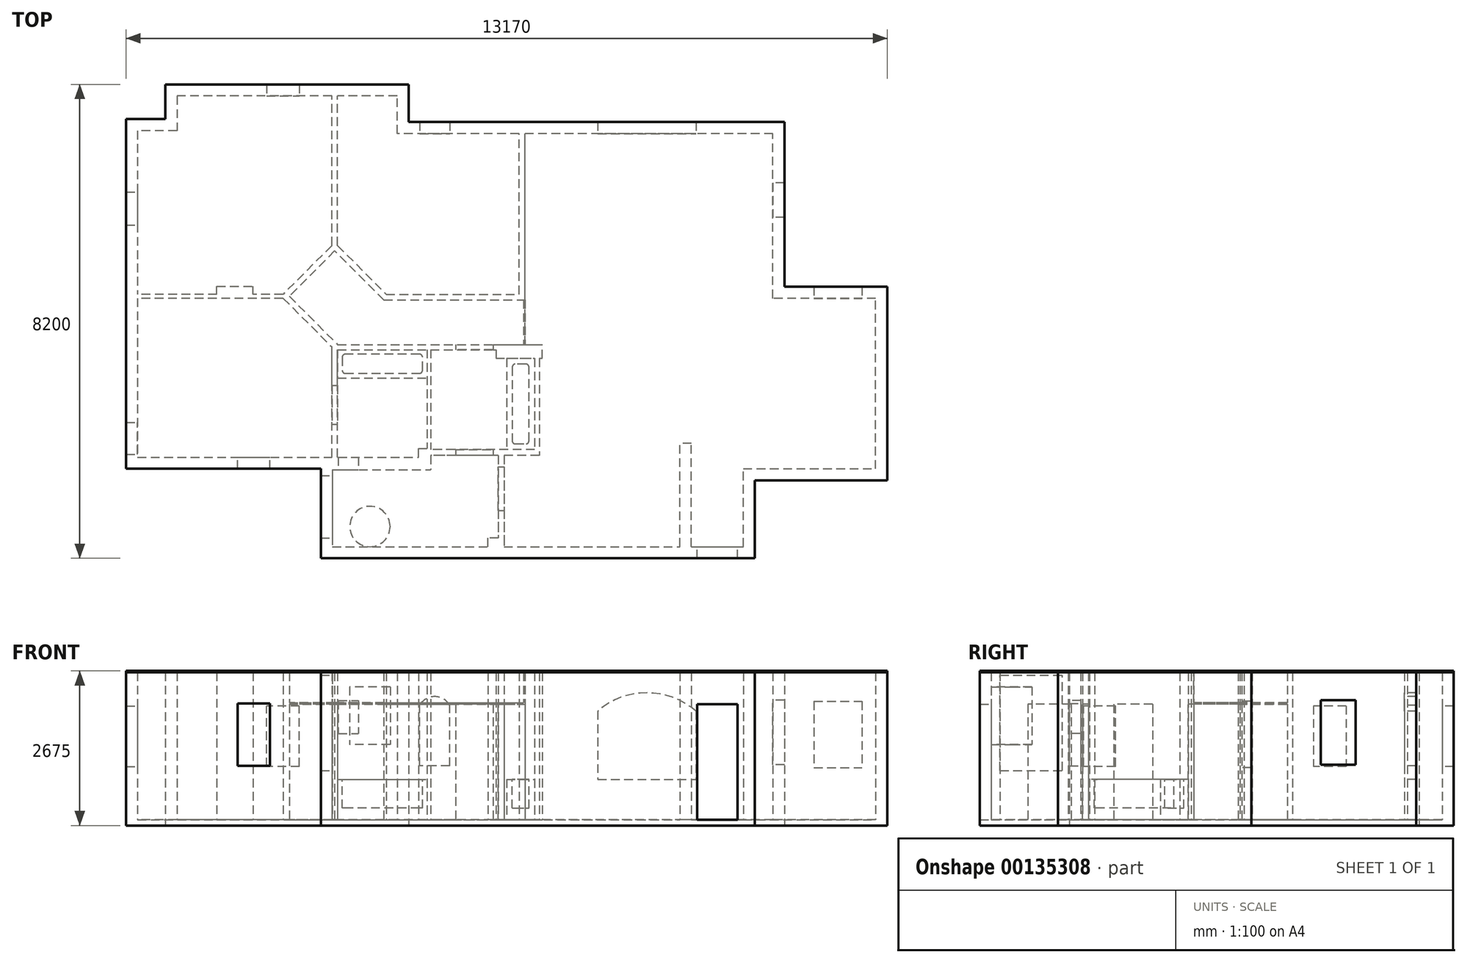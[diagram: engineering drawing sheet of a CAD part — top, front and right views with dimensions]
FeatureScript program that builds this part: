
annotation { "Feature Type Name" : "Feature", "Feature Type Description" : "" }
export const myFeature = defineFeature(function(context is Context, id is Id, definition is map)
    precondition{}
    {
        {
            var Q0;
            Q0=qCreatedBy(makeId("Top.planeOp"),FACE);
            var sketch = newSketch(context, id + "F0", { "sketchPlane" : qUnion([Q0])});
            skLineSegment(sketch, "E0", {"start": v(0, 0) * mm, "end": v(0, 1350) * mm});
            skLineSegment(sketch, "E1", {"start": v(0, 1350) * mm, "end": v(2290, 1350) * mm});
            skLineSegment(sketch, "E2", {"start": v(2290, 1350) * mm, "end": v(2290, 4300) * mm});
            skLineSegment(sketch, "E3", {"start": v(2290, 4300) * mm, "end": v(510, 4300) * mm});
            skLineSegment(sketch, "E4", {"start": v(510, 4300) * mm, "end": v(510, 7150) * mm});
            skLineSegment(sketch, "E5", {"start": v(510, 7150) * mm, "end": v(-5990, 7150) * mm});
            skLineSegment(sketch, "E6", {"start": v(-5990, 7150) * mm, "end": v(-5990, 7800) * mm});
            skLineSegment(sketch, "E7", {"start": v(-5990, 7800) * mm, "end": v(-9800, 7800) * mm});
            skLineSegment(sketch, "E8", {"start": v(-9800, 7800) * mm, "end": v(-9800, 7200) * mm});
            skLineSegment(sketch, "E9", {"start": v(-9800, 7200) * mm, "end": v(-10480, 7200) * mm});
            skLineSegment(sketch, "E10", {"start": v(-10480, 7200) * mm, "end": v(-10480, 1550) * mm});
            skLineSegment(sketch, "E11", {"start": v(-10480, 1550) * mm, "end": v(-7110, 1550) * mm});
            skLineSegment(sketch, "E12", {"start": v(-7110, 1550) * mm, "end": v(-7110, 0) * mm});
            skLineSegment(sketch, "E13", {"start": v(-7110, 0) * mm, "end": v(0, 0) * mm});
            skLineSegment(sketch, "E14.0", {"start": v(-5790, 7350) * mm, "end": v(-5790, 8000) * mm});
            skLineSegment(sketch, "E14.1", {"start": v(710, 7350) * mm, "end": v(-5790, 7350) * mm});
            skLineSegment(sketch, "E14.2", {"start": v(710, 4500) * mm, "end": v(710, 7350) * mm});
            skLineSegment(sketch, "E14.3", {"start": v(-10680, 1350) * mm, "end": v(-7310, 1350) * mm});
            skLineSegment(sketch, "E14.4", {"start": v(-10680, 7400) * mm, "end": v(-10680, 1350) * mm});
            skLineSegment(sketch, "E14.5", {"start": v(-10000, 7400) * mm, "end": v(-10680, 7400) * mm});
            skLineSegment(sketch, "E14.6", {"start": v(-10000, 8000) * mm, "end": v(-10000, 7400) * mm});
            skLineSegment(sketch, "E14.7", {"start": v(-7310, 1350) * mm, "end": v(-7310, -200) * mm});
            skLineSegment(sketch, "E14.8", {"start": v(-7310, -200) * mm, "end": v(200, -200) * mm});
            skLineSegment(sketch, "E14.9", {"start": v(200, -200) * mm, "end": v(200, 1150) * mm});
            skLineSegment(sketch, "E14.10", {"start": v(-5790, 8000) * mm, "end": v(-10000, 8000) * mm});
            skLineSegment(sketch, "E14.11", {"start": v(200, 1150) * mm, "end": v(2490, 1150) * mm});
            skLineSegment(sketch, "E14.12", {"start": v(2490, 1150) * mm, "end": v(2490, 4500) * mm});
            skLineSegment(sketch, "E14.13", {"start": v(2490, 4500) * mm, "end": v(710, 4500) * mm});
            skSolve(sketch);
        }
        {
            var Q0;
            Q0=makeQuery(id+"F0.imprint","IMPRINT",FACE,{"disambiguationData":[TD([[makeQuery(id+"F0.imprint","IMPRINT",EDGE,{"derivedFrom":sQuery(id+"F0.wireOp",EDGE,"E0")}),-1.0]])]});
            extrude(context, id + "F1", {"entities" : qUnion([Q0]), "depth" : 2550 * mm});
        }
        {
            var Q0;
            Q0=makeQuery(id+"F1.opExtrude","CAP_FACE",FACE,{"disambiguationData":[OSD([sQuery(id+"F0.wireOp",EDGE,"E0"),sQuery(id+"F0.wireOp",EDGE,"E1"),sQuery(id+"F0.wireOp",EDGE,"E2"),sQuery(id+"F0.wireOp",EDGE,"E3"),sQuery(id+"F0.wireOp",EDGE,"E4"),sQuery(id+"F0.wireOp",EDGE,"E5"),sQuery(id+"F0.wireOp",EDGE,"E6"),sQuery(id+"F0.wireOp",EDGE,"E7"),sQuery(id+"F0.wireOp",EDGE,"E8"),sQuery(id+"F0.wireOp",EDGE,"E9"),sQuery(id+"F0.wireOp",EDGE,"E10"),sQuery(id+"F0.wireOp",EDGE,"E11"),sQuery(id+"F0.wireOp",EDGE,"E12"),sQuery(id+"F0.wireOp",EDGE,"E13"),sQuery(id+"F0.wireOp",EDGE,"E14.0"),sQuery(id+"F0.wireOp",EDGE,"E14.1"),sQuery(id+"F0.wireOp",EDGE,"E14.2"),sQuery(id+"F0.wireOp",EDGE,"E14.3"),sQuery(id+"F0.wireOp",EDGE,"E14.4"),sQuery(id+"F0.wireOp",EDGE,"E14.5"),sQuery(id+"F0.wireOp",EDGE,"E14.6"),sQuery(id+"F0.wireOp",EDGE,"E14.7"),sQuery(id+"F0.wireOp",EDGE,"E14.8"),sQuery(id+"F0.wireOp",EDGE,"E14.9"),sQuery(id+"F0.wireOp",EDGE,"E14.10"),sQuery(id+"F0.wireOp",EDGE,"E14.11"),sQuery(id+"F0.wireOp",EDGE,"E14.12"),sQuery(id+"F0.wireOp",EDGE,"E14.13")])],"isStart":true});
            var sketch = newSketch(context, id + "F2", { "sketchPlane" : qUnion([Q0])});
            skLineSegment(sketch, "E15.0", {"start": v(-10000, -7400) * mm, "end": v(-10680, -7400) * mm});
            skLineSegment(sketch, "E15.1", {"start": v(-10680, -7400) * mm, "end": v(-10680, -1350) * mm});
            skLineSegment(sketch, "E15.2", {"start": v(-10680, -1350) * mm, "end": v(-7310, -1350) * mm});
            skLineSegment(sketch, "E15.3", {"start": v(-7310, -1350) * mm, "end": v(-7310, 200) * mm});
            skLineSegment(sketch, "E15.4", {"start": v(-7310, 200) * mm, "end": v(200, 200) * mm});
            skLineSegment(sketch, "E15.5", {"start": v(200, 200) * mm, "end": v(200, -1150) * mm});
            skLineSegment(sketch, "E15.6", {"start": v(200, -1150) * mm, "end": v(2490, -1150) * mm});
            skLineSegment(sketch, "E15.7", {"start": v(2490, -1150) * mm, "end": v(2490, -4500) * mm});
            skLineSegment(sketch, "E15.8", {"start": v(2490, -4500) * mm, "end": v(710, -4500) * mm});
            skLineSegment(sketch, "E15.9", {"start": v(710, -4500) * mm, "end": v(710, -7350) * mm});
            skLineSegment(sketch, "E15.10", {"start": v(710, -7350) * mm, "end": v(-5790, -7350) * mm});
            skLineSegment(sketch, "E15.11", {"start": v(-5790, -7350) * mm, "end": v(-5790, -8000) * mm});
            skLineSegment(sketch, "E15.12", {"start": v(-5790, -8000) * mm, "end": v(-10000, -8000) * mm});
            skLineSegment(sketch, "E15.13", {"start": v(-10000, -8000) * mm, "end": v(-10000, -7400) * mm});
            skSolve(sketch);
        }
        {
            var Q0;
            Q0=qSketchRegion(id+"F2",true);
            extrude(context, id + "F3", {"entities" : qUnion([Q0]), "operationType" : NewBodyOperationType.ADD, "depth" : 100 * mm});
        }
        {
            var Q0;
            Q0=qCreatedBy(makeId("Top.planeOp"),FACE);
            var sketch = newSketch(context, id + "F4", { "sketchPlane" : qUnion([Q0])});
            skLineSegment(sketch, "E16.right", {"start": v(-7120, 1550) * mm, "end": v(-7120, 3458.58) * mm});
            skLineSegment(sketch, "E17.bottom", {"start": v(-7961.42, 4370) * mm, "end": v(-10680, 4370) * mm});
            skLineSegment(sketch, "E17.top", {"start": v(-7961.42, 4300) * mm, "end": v(-10680, 4300) * mm});
            skLineSegment(sketch, "E18.trimOffspring", {"start": v(-7120, 5211.42) * mm, "end": v(-7120, 8000) * mm});
            skLineSegment(sketch, "E19", {"start": v(-6178.58, 4370) * mm, "end": v(-3880, 4370) * mm});
            skLineSegment(sketch, "E20", {"start": v(-3880, 4370) * mm, "end": v(-3880, 7350) * mm});
            skLineSegment(sketch, "E21.0", {"start": v(-3780, 4270) * mm, "end": v(-3780, 7350) * mm});
            skLineSegment(sketch, "E21.1", {"start": v(-6220, 4270) * mm, "end": v(-3780, 4270) * mm});
            skLineSegment(sketch, "E22.trimOffspring", {"start": v(-7020, 5211.42) * mm, "end": v(-7020, 8000) * mm});
            skLineSegment(sketch, "E23", {"start": v(-7020, 1550) * mm, "end": v(-7020, 3410) * mm});
            skLineSegment(sketch, "E24", {"start": v(-3880, 7350) * mm, "end": v(-3780, 7350) * mm});
            skLineSegment(sketch, "E25", {"start": v(-7120, 8000) * mm, "end": v(-7020, 8000) * mm});
            skLineSegment(sketch, "E26", {"start": v(-10680, 4370) * mm, "end": v(-10680, 4300) * mm});
            skLineSegment(sketch, "E27.bottom", {"start": v(-900, 0) * mm, "end": v(-1100, 0) * mm});
            skLineSegment(sketch, "E27.top", {"start": v(-900, 1790) * mm, "end": v(-1100, 1790) * mm});
            skLineSegment(sketch, "E27.left", {"start": v(-900, 0) * mm, "end": v(-900, 1790) * mm});
            skLineSegment(sketch, "E27.right", {"start": v(-1100, 0) * mm, "end": v(-1100, 1790) * mm});
            skLineSegment(sketch, "E28.bottom", {"start": v(-7020, 3500) * mm, "end": v(-3480, 3500) * mm});
            skLineSegment(sketch, "E28.top", {"start": v(-7020, 3410) * mm, "end": v(-4280, 3410) * mm});
            skLineSegment(sketch, "E29.bottom", {"start": v(-7020, 1550) * mm, "end": v(-5620, 1550) * mm});
            skLineSegment(sketch, "E29.top", {"start": v(-7110, 1330) * mm, "end": v(-5410, 1330) * mm});
            skLineSegment(sketch, "E29.left", {"start": v(-7110, 1550) * mm, "end": v(-7110, 1330) * mm});
            skLineSegment(sketch, "E29.right", {"start": v(-5410, 1550) * mm, "end": v(-5410, 1330) * mm});
            skLineSegment(sketch, "E30.bottom", {"start": v(-5410, 3410) * mm, "end": v(-5470, 3410) * mm});
            skLineSegment(sketch, "E30.left", {"start": v(-5410, 3410) * mm, "end": v(-5410, 1680) * mm});
            skLineSegment(sketch, "E30.right", {"start": v(-5470, 3410) * mm, "end": v(-5470, 1700) * mm});
            skLineSegment(sketch, "E31.top", {"start": v(-3610, 1680) * mm, "end": v(-3530, 1680) * mm});
            skLineSegment(sketch, "E31.left", {"start": v(-3610, 3260) * mm, "end": v(-3610, 1680) * mm});
            skLineSegment(sketch, "E31.right", {"start": v(-3530, 3260) * mm, "end": v(-3530, 1680) * mm});
            skLineSegment(sketch, "E32.bottom", {"start": v(-3530, 1680) * mm, "end": v(-5410, 1680) * mm});
            skLineSegment(sketch, "E32.top", {"start": v(-3530, 1580) * mm, "end": v(-5410, 1580) * mm});
            skLineSegment(sketch, "E32.left", {"start": v(-3530, 1680) * mm, "end": v(-3530, 1580) * mm});
            skLineSegment(sketch, "E33.bottom", {"start": v(-9110, 4370) * mm, "end": v(-8480, 4370) * mm});
            skLineSegment(sketch, "E33.top", {"start": v(-9110, 4510) * mm, "end": v(-8480, 4510) * mm});
            skLineSegment(sketch, "E33.left", {"start": v(-9110, 4370) * mm, "end": v(-9110, 4510) * mm});
            skLineSegment(sketch, "E33.right", {"start": v(-8480, 4370) * mm, "end": v(-8480, 4510) * mm});
            skLineSegment(sketch, "E34.top", {"start": v(-4280, 3260) * mm, "end": v(-3610, 3260) * mm});
            skLineSegment(sketch, "E34.left", {"start": v(-4280, 3410) * mm, "end": v(-4280, 3260) * mm});
            skLineSegment(sketch, "E35.trimOffspring", {"start": v(-3530, 3260) * mm, "end": v(-3480, 3260) * mm});
            skLineSegment(sketch, "E36.trimOffspring", {"start": v(-5410, 1580) * mm, "end": v(-5410, 1550) * mm});
            skLineSegment(sketch, "E37.bottom", {"start": v(-4240, 1580) * mm, "end": v(-4140, 1580) * mm});
            skLineSegment(sketch, "E37.left", {"start": v(-4240, 1580) * mm, "end": v(-4240, 150) * mm});
            skLineSegment(sketch, "E37.right", {"start": v(-4140, 1580) * mm, "end": v(-4140, 0) * mm});
            skLineSegment(sketch, "E38.top", {"start": v(-4240, 150) * mm, "end": v(-4420, 150) * mm});
            skLineSegment(sketch, "E38.right", {"start": v(-4420, 0) * mm, "end": v(-4420, 150) * mm});
            skLineSegment(sketch, "E39", {"start": v(-4420, 0) * mm, "end": v(-4140, 0) * mm});
            skLineSegment(sketch, "E40", {"start": v(-7120, 1550) * mm, "end": v(-7110, 1550) * mm});
            skLineSegment(sketch, "E41", {"start": v(-7020, 5211.42) * mm, "end": v(-6178.58, 4370) * mm});
            skLineSegment(sketch, "E42", {"start": v(-7120, 5211.42) * mm, "end": v(-7961.42, 4370) * mm});
            skLineSegment(sketch, "E43", {"start": v(-7961.42, 4300) * mm, "end": v(-7120, 3458.58) * mm});
            skLineSegment(sketch, "E44", {"start": v(-6220, 4270) * mm, "end": v(-7070, 5120) * mm});
            skLineSegment(sketch, "E45", {"start": v(-7070, 5120) * mm, "end": v(-7855, 4335) * mm});
            skLineSegment(sketch, "E46", {"start": v(-7855, 4335) * mm, "end": v(-7020, 3500) * mm});
            skLineSegment(sketch, "E47", {"start": v(-7961.42, 4370) * mm, "end": v(-7961.42, 4300) * mm, "construction": true});
            skLineSegment(sketch, "E48", {"start": v(-7961.42, 4335) * mm, "end": v(-7620.59, 4335) * mm, "construction": true});
            skLineSegment(sketch, "E49", {"start": v(-3480, 3260) * mm, "end": v(-3480, 3500) * mm});
            skLineSegment(sketch, "E50", {"start": v(-5620, 1550) * mm, "end": v(-5620, 1700) * mm});
            skLineSegment(sketch, "E51", {"start": v(-5620, 1700) * mm, "end": v(-5470, 1700) * mm});
            skSolve(sketch);
        }
        {
            var Q0;
            Q0=qSketchRegion(id+"F4",true);
            extrude(context, id + "F5", {"entities" : qUnion([Q0]), "operationType" : NewBodyOperationType.ADD, "depth" : 2550 * mm});
        }
        {
            var Q0;
            Q0=makeQuery(id+"F1.opExtrude","SWEPT_FACE",FACE,{"disambiguationData":[OSD([sQuery(id+"F0.wireOp",EDGE,"E3")])]});
            var sketch = newSketch(context, id + "F6", { "sketchPlane" : qUnion([Q0])});
            skLineSegment(sketch, "E52.bottom", {"start": v(1220, 2050) * mm, "end": v(2050, 2050) * mm});
            skLineSegment(sketch, "E52.top", {"start": v(1220, 900) * mm, "end": v(2050, 900) * mm});
            skLineSegment(sketch, "E52.left", {"start": v(1220, 2050) * mm, "end": v(1220, 900) * mm});
            skLineSegment(sketch, "E52.right", {"start": v(2050, 2050) * mm, "end": v(2050, 900) * mm});
            skSolve(sketch);
        }
        {
            var Q0;
            Q0=qSketchRegion(id+"F6",true);
            extrude(context, id + "F7", {"entities" : qUnion([Q0]), "operationType" : NewBodyOperationType.REMOVE, "endBound" : BoundingType.THROUGH_ALL, "oppositeDirection" : true, "depth" : 25 * mm});
        }
        {
            var Q0;
            Q0=makeQuery(id+"F1.opExtrude","SWEPT_FACE",FACE,{"disambiguationData":[OSD([sQuery(id+"F0.wireOp",EDGE,"E4")])]});
            var sketch = newSketch(context, id + "F8", { "sketchPlane" : qUnion([Q0])});
            skLineSegment(sketch, "E53.bottom", {"start": v(-6300, 950) * mm, "end": v(-5700, 950) * mm});
            skLineSegment(sketch, "E53.top", {"start": v(-6300, 2070) * mm, "end": v(-5700, 2070) * mm});
            skLineSegment(sketch, "E53.left", {"start": v(-6300, 950) * mm, "end": v(-6300, 2070) * mm});
            skLineSegment(sketch, "E53.right", {"start": v(-5700, 950) * mm, "end": v(-5700, 2070) * mm});
            skSolve(sketch);
        }
        {
            var Q0;
            Q0=qSketchRegion(id+"F8",true);
            extrude(context, id + "F9", {"entities" : qUnion([Q0]), "operationType" : NewBodyOperationType.REMOVE, "endBound" : BoundingType.UP_TO_NEXT, "oppositeDirection" : true, "depth" : 25 * mm});
        }
        {
            var Q0;
            {var subQ1=sQuery(id+"F0.wireOp",EDGE,"E4");var subQ2=sQuery(id+"F0.wireOp",EDGE,"E5");Q0=makeQuery(id+"F5.boolean.opBoolean","SPLIT",FACE,{"disambiguationData":[TD([makeQuery(id+"F1.opExtrude","SWEPT_FACE",FACE,{"disambiguationData":[OSD([subQ1])]})])],"derivedFrom":makeQuery(id+"F1.opExtrude","SWEPT_FACE",FACE,{"disambiguationData":[OSD([subQ2])]})});}
            var sketch = newSketch(context, id + "F10", { "sketchPlane" : qUnion([Q0])});
            skLineSegment(sketch, "E54.top", {"start": v(-2520, 700) * mm, "end": v(-820, 700) * mm});
            skLineSegment(sketch, "E54.left", {"start": v(-2520, 1880) * mm, "end": v(-2520, 700) * mm});
            skLineSegment(sketch, "E54.right", {"start": v(-820, 1880) * mm, "end": v(-820, 700) * mm});
            skArc(sketch, "E55", {"start": v(-820, 1880) * mm, "mid": v(-1670, 2196.38) * mm, "end": v(-2520, 1880) * mm});
            skSolve(sketch);
        }
        {
            var Q0;
            Q0=qSketchRegion(id+"F10",true);
            extrude(context, id + "F11", {"entities" : qUnion([Q0]), "operationType" : NewBodyOperationType.REMOVE, "endBound" : BoundingType.UP_TO_NEXT, "oppositeDirection" : true, "depth" : 25 * mm});
        }
        {
            var Q0;
            {var subQ1=sQuery(id+"F0.wireOp",EDGE,"E6");var subQ2=sQuery(id+"F0.wireOp",EDGE,"E5");Q0=makeQuery(id+"F5.boolean.opBoolean","SPLIT",FACE,{"disambiguationData":[TD([makeQuery(id+"F1.opExtrude","SWEPT_FACE",FACE,{"disambiguationData":[OSD([subQ1])]})])],"derivedFrom":makeQuery(id+"F1.opExtrude","SWEPT_FACE",FACE,{"disambiguationData":[OSD([subQ2])]})});}
            var sketch = newSketch(context, id + "F12", { "sketchPlane" : qUnion([Q0])});
            skLineSegment(sketch, "E56.top", {"start": v(-5600, 930) * mm, "end": v(-5080, 930) * mm});
            skLineSegment(sketch, "E56.left", {"start": v(-5600, 1980) * mm, "end": v(-5600, 930) * mm});
            skLineSegment(sketch, "E56.right", {"start": v(-5080, 1980) * mm, "end": v(-5080, 930) * mm});
            skArc(sketch, "E57", {"start": v(-5080, 1980) * mm, "mid": v(-5340, 2130.33) * mm, "end": v(-5600, 1980) * mm});
            skSolve(sketch);
        }
        {
            var Q0;
            Q0=qSketchRegion(id+"F12",true);
            extrude(context, id + "F13", {"entities" : qUnion([Q0]), "operationType" : NewBodyOperationType.REMOVE, "endBound" : BoundingType.UP_TO_NEXT, "oppositeDirection" : true, "depth" : 25 * mm});
        }
        {
            var Q0;
            {var subQ1=sQuery(id+"F0.wireOp",EDGE,"E8");var subQ2=sQuery(id+"F0.wireOp",EDGE,"E7");Q0=makeQuery(id+"F5.boolean.opBoolean","SPLIT",FACE,{"disambiguationData":[TD([makeQuery(id+"F1.opExtrude","SWEPT_FACE",FACE,{"disambiguationData":[OSD([subQ1])]})])],"derivedFrom":makeQuery(id+"F1.opExtrude","SWEPT_FACE",FACE,{"disambiguationData":[OSD([subQ2])]})});}
            var sketch = newSketch(context, id + "F14", { "sketchPlane" : qUnion([Q0])});
            skLineSegment(sketch, "E58.bottom", {"start": v(-8250, 1970) * mm, "end": v(-7680, 1970) * mm});
            skLineSegment(sketch, "E58.top", {"start": v(-8250, 920) * mm, "end": v(-7680, 920) * mm});
            skLineSegment(sketch, "E58.left", {"start": v(-8250, 1970) * mm, "end": v(-8250, 920) * mm});
            skLineSegment(sketch, "E58.right", {"start": v(-7680, 1970) * mm, "end": v(-7680, 920) * mm});
            skSolve(sketch);
        }
        {
            var Q0;
            Q0=qSketchRegion(id+"F14",true);
            extrude(context, id + "F15", {"entities" : qUnion([Q0]), "operationType" : NewBodyOperationType.REMOVE, "endBound" : BoundingType.UP_TO_NEXT, "oppositeDirection" : true, "depth" : 25 * mm});
        }
        {
            var Q0;
            {var subQ3=sQuery(id+"F0.wireOp",EDGE,"E9");var subQ4=sQuery(id+"F0.wireOp",EDGE,"E10");Q0=makeQuery(id+"F5.boolean.opBoolean","SPLIT",FACE,{"disambiguationData":[TD([makeQuery(id+"F1.opExtrude","SWEPT_FACE",FACE,{"disambiguationData":[OSD([subQ3])]})])],"derivedFrom":makeQuery(id+"F1.opExtrude","SWEPT_FACE",FACE,{"disambiguationData":[OSD([subQ4])]})});}
            var sketch = newSketch(context, id + "F16", { "sketchPlane" : qUnion([Q0])});
            skLineSegment(sketch, "E59.bottom", {"start": v(6140, 1970) * mm, "end": v(5570, 1970) * mm});
            skLineSegment(sketch, "E59.top", {"start": v(6140, 920) * mm, "end": v(5570, 920) * mm});
            skLineSegment(sketch, "E59.left", {"start": v(6140, 1970) * mm, "end": v(6140, 920) * mm});
            skLineSegment(sketch, "E59.right", {"start": v(5570, 1970) * mm, "end": v(5570, 920) * mm});
            skSolve(sketch);
        }
        {
            var Q0;
            Q0=qSketchRegion(id+"F16",true);
            extrude(context, id + "F17", {"entities" : qUnion([Q0]), "operationType" : NewBodyOperationType.REMOVE, "endBound" : BoundingType.UP_TO_NEXT, "oppositeDirection" : true, "depth" : 25 * mm});
        }
        {
            var Q0;
            {var subQ4=sQuery(id+"F0.wireOp",EDGE,"E11");var subQ5=sQuery(id+"F0.wireOp",EDGE,"E10");Q0=makeQuery(id+"F5.boolean.opBoolean","SPLIT",FACE,{"disambiguationData":[TD([makeQuery(id+"F1.opExtrude","SWEPT_FACE",FACE,{"disambiguationData":[OSD([subQ4])]})])],"derivedFrom":makeQuery(id+"F1.opExtrude","SWEPT_FACE",FACE,{"disambiguationData":[OSD([subQ5])]})});}
            var sketch = newSketch(context, id + "F18", { "sketchPlane" : qUnion([Q0])});
            skLineSegment(sketch, "E60.bottom", {"start": v(1600, 1970) * mm, "end": v(2150, 1970) * mm});
            skLineSegment(sketch, "E60.top", {"start": v(1600, 920) * mm, "end": v(2150, 920) * mm});
            skLineSegment(sketch, "E60.left", {"start": v(1600, 1970) * mm, "end": v(1600, 920) * mm});
            skLineSegment(sketch, "E60.right", {"start": v(2150, 1970) * mm, "end": v(2150, 920) * mm});
            skSolve(sketch);
        }
        {
            var Q0;
            Q0=qSketchRegion(id+"F18",true);
            extrude(context, id + "F19", {"entities" : qUnion([Q0]), "operationType" : NewBodyOperationType.REMOVE, "endBound" : BoundingType.UP_TO_NEXT, "oppositeDirection" : true, "depth" : 25 * mm});
        }
        {
            var Q0;
            Q0=makeQuery(id+"F1.opExtrude","SWEPT_FACE",FACE,{"disambiguationData":[OSD([sQuery(id+"F0.wireOp",EDGE,"E11")])]});
            var sketch = newSketch(context, id + "F20", { "sketchPlane" : qUnion([Q0])});
            skLineSegment(sketch, "E61.bottom", {"start": v(8750, 2010) * mm, "end": v(8190, 2010) * mm});
            skLineSegment(sketch, "E61.top", {"start": v(8750, 930) * mm, "end": v(8190, 930) * mm});
            skLineSegment(sketch, "E61.left", {"start": v(8750, 2010) * mm, "end": v(8750, 930) * mm});
            skLineSegment(sketch, "E61.right", {"start": v(8190, 2010) * mm, "end": v(8190, 930) * mm});
            skSolve(sketch);
        }
        {
            var Q0;
            Q0=qSketchRegion(id+"F20",true);
            extrude(context, id + "F21", {"entities" : qUnion([Q0]), "operationType" : NewBodyOperationType.REMOVE, "endBound" : BoundingType.UP_TO_NEXT, "oppositeDirection" : true, "depth" : 25 * mm});
        }
        {
            var Q0;
            Q0=makeQuery(id+"F1.opExtrude","SWEPT_FACE",FACE,{"disambiguationData":[OSD([sQuery(id+"F0.wireOp",EDGE,"E12")])]});
            var sketch = newSketch(context, id + "F22", { "sketchPlane" : qUnion([Q0])});
            skLineSegment(sketch, "E62.bottom", {"start": v(1230, 2500) * mm, "end": v(150, 2500) * mm});
            skLineSegment(sketch, "E62.top", {"start": v(1230, 850) * mm, "end": v(150, 850) * mm});
            skLineSegment(sketch, "E62.left", {"start": v(1230, 2500) * mm, "end": v(1230, 850) * mm});
            skLineSegment(sketch, "E62.right", {"start": v(150, 2500) * mm, "end": v(150, 850) * mm});
            skSolve(sketch);
        }
        {
            var Q0;
            Q0=qSketchRegion(id+"F22",true);
            extrude(context, id + "F23", {"entities" : qUnion([Q0]), "operationType" : NewBodyOperationType.REMOVE, "endBound" : BoundingType.UP_TO_NEXT, "oppositeDirection" : true, "depth" : 25 * mm});
        }
        {
            var Q0;
            Q0=makeQuery(id+"F5.opExtrude","SWEPT_FACE",FACE,{"disambiguationData":[OSD([sQuery(id+"F4.wireOp",EDGE,"E29.top")])]});
            var sketch = newSketch(context, id + "F24", { "sketchPlane" : qUnion([Q0])});
            skLineSegment(sketch, "E63.bottom", {"start": v(-7010, 2060) * mm, "end": v(-6660, 2060) * mm});
            skLineSegment(sketch, "E63.top", {"start": v(-7010, 1490) * mm, "end": v(-6660, 1490) * mm});
            skLineSegment(sketch, "E63.left", {"start": v(-7010, 2060) * mm, "end": v(-7010, 1490) * mm});
            skLineSegment(sketch, "E63.right", {"start": v(-6660, 2060) * mm, "end": v(-6660, 1490) * mm});
            skSolve(sketch);
        }
        {
            var Q0;
            Q0=qSketchRegion(id+"F24",true);
            extrude(context, id + "F25", {"entities" : qUnion([Q0]), "operationType" : NewBodyOperationType.REMOVE, "endBound" : BoundingType.UP_TO_NEXT, "oppositeDirection" : true, "depth" : 25 * mm});
        }
        {
            var Q0;
            {var subQ0=sQuery(id+"F4.wireOp",EDGE,"E23");Q0=makeQuery(id+"F25.boolean.opBoolean","MERGE",FACE,{"derivedFrom":[makeQuery(id+"F5.opExtrude","SWEPT_FACE",FACE,{"disambiguationData":[OSD([subQ0]),TDD([makeQuery(id+"F4.imprint","IMPRINT",EDGE,{"disambiguationData":[TD([[makeQuery(id+"F4.imprint","INTERSECT",VERTEX,{"derivedFrom":[subQ0,sQuery(id+"F4.wireOp",EDGE,"E29.bottom")]}),-1.0]])],"derivedFrom":subQ0})])]}),makeQuery(id+"F25.opExtrude","SWEPT_FACE",FACE,{"disambiguationData":[OSD([sQuery(id+"F24.wireOp",EDGE,"E63.left")])]})]});}
            var sketch = newSketch(context, id + "F26", { "sketchPlane" : qUnion([Q0])});
            skLineSegment(sketch, "E64.bottom", {"start": v(2790, 2000) * mm, "end": v(2120, 2000) * mm});
            skLineSegment(sketch, "E64.top", {"start": v(2790, 0) * mm, "end": v(2120, 0) * mm});
            skLineSegment(sketch, "E64.left", {"start": v(2790, 2000) * mm, "end": v(2790, 0) * mm});
            skLineSegment(sketch, "E64.right", {"start": v(2120, 2000) * mm, "end": v(2120, 0) * mm});
            skSolve(sketch);
        }
        {
            var Q0;
            Q0=makeQuery(id+"F26.imprint","IMPRINT",FACE,{"disambiguationData":[TD([[makeQuery(id+"F26.imprint","IMPRINT",EDGE,{"derivedFrom":sQuery(id+"F26.wireOp",EDGE,"E64.bottom")}),1.0]])]});
            extrude(context, id + "F27", {"entities" : qUnion([Q0]), "operationType" : NewBodyOperationType.REMOVE, "endBound" : BoundingType.UP_TO_NEXT, "oppositeDirection" : true, "depth" : 25 * mm});
        }
        {
            var Q0;
            {var subQ0=sQuery(id+"F4.wireOp",EDGE,"E28.top");Q0=makeQuery(id+"F5.opExtrude","SWEPT_FACE",FACE,{"disambiguationData":[OSD([subQ0]),TDD([makeQuery(id+"F4.imprint","IMPRINT",EDGE,{"disambiguationData":[TD([[makeQuery(id+"F4.imprint","INTERSECT",VERTEX,{"derivedFrom":[subQ0,sQuery(id+"F4.wireOp",EDGE,"E30.bottom"),sQuery(id+"F4.wireOp",EDGE,"E30.left")]}),-1.0]])],"derivedFrom":subQ0})])]});}
            var sketch = newSketch(context, id + "F28", { "sketchPlane" : qUnion([Q0])});
            skLineSegment(sketch, "E65.bottom", {"start": v(-4980, 2000) * mm, "end": v(-4330, 2000) * mm});
            skLineSegment(sketch, "E65.top", {"start": v(-4980, 0) * mm, "end": v(-4330, 0) * mm});
            skLineSegment(sketch, "E65.left", {"start": v(-4980, 2000) * mm, "end": v(-4980, 0) * mm});
            skLineSegment(sketch, "E65.right", {"start": v(-4330, 2000) * mm, "end": v(-4330, 0) * mm});
            skSolve(sketch);
        }
        {
            var Q0;
            Q0=qSketchRegion(id+"F28",true);
            var Q1;
            Q1=makeQuery(id+"F5.opExtrude","SWEPT_FACE",FACE,{"disambiguationData":[OSD([sQuery(id+"F4.wireOp",EDGE,"E32.top")])]});
            extrude(context, id + "F29", {"entities" : qUnion([Q0]), "operationType" : NewBodyOperationType.REMOVE, "endBound" : BoundingType.UP_TO_NEXT, "oppositeDirection" : true, "depth" : 25 * mm, "hasSecondDirection" : true, "secondDirectionBound" : BoundingType.UP_TO_SURFACE, "secondDirectionOppositeDirection" : false, "secondDirectionBoundEntityFace" : qUnion([Q1]), "secondDirectionDepth" : 25 * mm});
        }
        {
            var Q0;
            {var subQ0=sQuery(id+"F0.wireOp",EDGE,"E13");var subQ1=sQuery(id+"F0.wireOp",EDGE,"E0");Q0=makeQuery(id+"F5.boolean.opBoolean","SPLIT",FACE,{"disambiguationData":[TD([makeQuery(id+"F1.opExtrude","SWEPT_FACE",FACE,{"disambiguationData":[OSD([subQ1])]})])],"derivedFrom":makeQuery(id+"F1.opExtrude","SWEPT_FACE",FACE,{"disambiguationData":[OSD([subQ0])]})});}
            var sketch = newSketch(context, id + "F30", { "sketchPlane" : qUnion([Q0])});
            skLineSegment(sketch, "E66.bottom", {"start": v(800, 2000) * mm, "end": v(100, 2000) * mm});
            skLineSegment(sketch, "E66.top", {"start": v(800, 0) * mm, "end": v(100, 0) * mm});
            skLineSegment(sketch, "E66.left", {"start": v(800, 2000) * mm, "end": v(800, 0) * mm});
            skLineSegment(sketch, "E66.right", {"start": v(100, 2000) * mm, "end": v(100, 0) * mm});
            skSolve(sketch);
        }
        {
            var Q0;
            Q0=makeQuery(id+"F30.imprint","IMPRINT",FACE,{"disambiguationData":[TD([[makeQuery(id+"F30.imprint","IMPRINT",EDGE,{"derivedFrom":sQuery(id+"F30.wireOp",EDGE,"E66.bottom")}),1.0]])]});
            extrude(context, id + "F31", {"entities" : qUnion([Q0]), "operationType" : NewBodyOperationType.REMOVE, "endBound" : BoundingType.UP_TO_NEXT, "oppositeDirection" : true, "depth" : 25 * mm});
        }
        {
            var Q0;
            Q0=makeQuery(id+"F5.opExtrude","SWEPT_FACE",FACE,{"disambiguationData":[OSD([sQuery(id+"F4.wireOp",EDGE,"E37.right")])]});
            var sketch = newSketch(context, id + "F32", { "sketchPlane" : qUnion([Q0])});
            skLineSegment(sketch, "E67.bottom", {"start": v(1380, 2000) * mm, "end": v(630, 2000) * mm});
            skLineSegment(sketch, "E67.top", {"start": v(1380, 0) * mm, "end": v(630, 0) * mm});
            skLineSegment(sketch, "E67.left", {"start": v(1380, 2000) * mm, "end": v(1380, 0) * mm});
            skLineSegment(sketch, "E67.right", {"start": v(630, 2000) * mm, "end": v(630, 0) * mm});
            skSolve(sketch);
        }
        {
            var Q0;
            Q0=qSketchRegion(id+"F32",true);
            extrude(context, id + "F33", {"entities" : qUnion([Q0]), "operationType" : NewBodyOperationType.REMOVE, "endBound" : BoundingType.UP_TO_NEXT, "oppositeDirection" : true, "depth" : 25 * mm});
        }
        {
            var Q0;
            Q0=qCreatedBy(makeId("Top.planeOp"),FACE);
            cPlane(context, id + "F34", {"entities" : qUnion([Q0]), "cplaneType" : CPlaneType.OFFSET, "offset" : 2000 * mm, "width" : 150 * mm, "height" : 150 * mm});
        }
        {
            var Q0;
            Q0=qCreatedBy(id+"F34.planeOp",FACE);
            var sketch = newSketch(context, id + "F35", { "sketchPlane" : qUnion([Q0])});
            skLineSegment(sketch, "E68.0", {"start": v(-6220, 4270) * mm, "end": v(-3780, 4270) * mm});
            skLineSegment(sketch, "E69.0", {"start": v(-6220, 4270) * mm, "end": v(-7070, 5120) * mm});
            skLineSegment(sketch, "E70.0", {"start": v(-7070, 5120) * mm, "end": v(-7855, 4335) * mm});
            skLineSegment(sketch, "E71.0", {"start": v(-7855, 4335) * mm, "end": v(-7020, 3500) * mm});
            skLineSegment(sketch, "E72.0", {"start": v(-7020, 3500) * mm, "end": v(-3780, 3500) * mm});
            skLineSegment(sketch, "E73", {"start": v(-3780, 4270) * mm, "end": v(-3780, 3500) * mm});
            skSolve(sketch);
        }
        {
            var Q0;
            Q0=qSketchRegion(id+"F35",true);
            extrude(context, id + "F36", {"entities" : qUnion([Q0]), "operationType" : NewBodyOperationType.ADD, "depth" : 25 * mm});
        }
        {
            var Q0;
            Q0=makeQuery(id+"F36.boolean.opBoolean","MERGE",FACE,{"derivedFrom":[makeQuery(id+"F5.opExtrude","SWEPT_FACE",FACE,{"disambiguationData":[OSD([sQuery(id+"F4.wireOp",EDGE,"E21.0")])]}),makeQuery(id+"F36.opExtrude","SWEPT_FACE",FACE,{"disambiguationData":[OSD([sQuery(id+"F35.wireOp",EDGE,"zDjcXcot-WBPH-Oz7D-FypC-yUx7rtA3DrP4")])]})]});
            var sketch = newSketch(context, id + "F37", { "sketchPlane" : qUnion([Q0])});
            skLineSegment(sketch, "E74.0", {"start": v(4270, 2550) * mm, "end": v(4270, 2025) * mm});
            skLineSegment(sketch, "E75.0", {"start": v(4270, 2025) * mm, "end": v(3500, 2025) * mm});
            skLineSegment(sketch, "E76", {"start": v(3500, 2025) * mm, "end": v(3500, 2550) * mm});
            skLineSegment(sketch, "E77", {"start": v(4270, 2550) * mm, "end": v(3500, 2550) * mm});
            skSolve(sketch);
        }
        {
            var Q0;
            Q0=qSketchRegion(id+"F37",true);
            extrude(context, id + "F38", {"entities" : qUnion([Q0]), "operationType" : NewBodyOperationType.ADD, "oppositeDirection" : true, "depth" : 25 * mm});
        }
        {
            var Q0;
            Q0=makeQuery(id+"F5.boolean.opBoolean","MERGE",FACE,{"derivedFrom":[makeQuery(id+"F1.opExtrude","CAP_FACE",FACE,{"disambiguationData":[OSD([sQuery(id+"F0.wireOp",EDGE,"E0"),sQuery(id+"F0.wireOp",EDGE,"E1"),sQuery(id+"F0.wireOp",EDGE,"E2"),sQuery(id+"F0.wireOp",EDGE,"E3"),sQuery(id+"F0.wireOp",EDGE,"E4"),sQuery(id+"F0.wireOp",EDGE,"E5"),sQuery(id+"F0.wireOp",EDGE,"E6"),sQuery(id+"F0.wireOp",EDGE,"E7"),sQuery(id+"F0.wireOp",EDGE,"E8"),sQuery(id+"F0.wireOp",EDGE,"E9"),sQuery(id+"F0.wireOp",EDGE,"E10"),sQuery(id+"F0.wireOp",EDGE,"E11"),sQuery(id+"F0.wireOp",EDGE,"E12"),sQuery(id+"F0.wireOp",EDGE,"E13"),sQuery(id+"F0.wireOp",EDGE,"E14.0"),sQuery(id+"F0.wireOp",EDGE,"E14.1"),sQuery(id+"F0.wireOp",EDGE,"E14.2"),sQuery(id+"F0.wireOp",EDGE,"E14.3"),sQuery(id+"F0.wireOp",EDGE,"E14.4"),sQuery(id+"F0.wireOp",EDGE,"E14.5"),sQuery(id+"F0.wireOp",EDGE,"E14.6"),sQuery(id+"F0.wireOp",EDGE,"E14.7"),sQuery(id+"F0.wireOp",EDGE,"E14.8"),sQuery(id+"F0.wireOp",EDGE,"E14.9"),sQuery(id+"F0.wireOp",EDGE,"E14.10"),sQuery(id+"F0.wireOp",EDGE,"E14.11"),sQuery(id+"F0.wireOp",EDGE,"E14.12"),sQuery(id+"F0.wireOp",EDGE,"E14.13")])],"isStart":false}),makeQuery(id+"F5.opExtrude","CAP_FACE",FACE,{"disambiguationData":[OSD([sQuery(id+"F4.wireOp",EDGE,"E16.right"),sQuery(id+"F4.wireOp",EDGE,"E17.bottom"),sQuery(id+"F4.wireOp",EDGE,"E17.top"),sQuery(id+"F4.wireOp",EDGE,"E18.trimOffspring"),sQuery(id+"F4.wireOp",EDGE,"HC3yR3A7-nPZG-II4q-koSb-6mGTPuyd2gmC"),sQuery(id+"F4.wireOp",EDGE,"K4PCeNqw-pmFu-T04N-sqqH-EL8HlTzb0BrP"),sQuery(id+"F4.wireOp",EDGE,"E19"),sQuery(id+"F4.wireOp",EDGE,"E20"),sQuery(id+"F4.wireOp",EDGE,"E21.0"),sQuery(id+"F4.wireOp",EDGE,"E21.1"),sQuery(id+"F4.wireOp",EDGE,"E21.2"),sQuery(id+"F4.wireOp",EDGE,"E21.3"),sQuery(id+"F4.wireOp",EDGE,"E22.trimOffspring"),sQuery(id+"F4.wireOp",EDGE,"E23"),sQuery(id+"F4.wireOp",EDGE,"E24"),sQuery(id+"F4.wireOp",EDGE,"E25"),sQuery(id+"F4.wireOp",EDGE,"E26"),sQuery(id+"F4.wireOp",EDGE,"E28.bottom"),sQuery(id+"F4.wireOp",EDGE,"E28.top"),sQuery(id+"F4.wireOp",EDGE,"E28.right"),sQuery(id+"F4.wireOp",EDGE,"E29.bottom"),sQuery(id+"F4.wireOp",EDGE,"E29.top"),sQuery(id+"F4.wireOp",EDGE,"E29.left"),sQuery(id+"F4.wireOp",EDGE,"E29.right"),sQuery(id+"F4.wireOp",EDGE,"E30.left"),sQuery(id+"F4.wireOp",EDGE,"E30.right"),sQuery(id+"F4.wireOp",EDGE,"E31.left"),sQuery(id+"F4.wireOp",EDGE,"E31.right"),sQuery(id+"F4.wireOp",EDGE,"E32.bottom"),sQuery(id+"F4.wireOp",EDGE,"E32.top"),sQuery(id+"F4.wireOp",EDGE,"E32.left"),sQuery(id+"F4.wireOp",EDGE,"E33.top"),sQuery(id+"F4.wireOp",EDGE,"E33.left"),sQuery(id+"F4.wireOp",EDGE,"E33.right"),sQuery(id+"F4.wireOp",EDGE,"E34.top"),sQuery(id+"F4.wireOp",EDGE,"E34.left"),sQuery(id+"F4.wireOp",EDGE,"E34.right"),sQuery(id+"F4.wireOp",EDGE,"E35.trimOffspring"),sQuery(id+"F4.wireOp",EDGE,"E36.trimOffspring"),sQuery(id+"F4.wireOp",EDGE,"E37.left"),sQuery(id+"F4.wireOp",EDGE,"E37.right"),sQuery(id+"F4.wireOp",EDGE,"E38.top"),sQuery(id+"F4.wireOp",EDGE,"E38.right"),sQuery(id+"F4.wireOp",EDGE,"E39"),sQuery(id+"F4.wireOp",EDGE,"E40")])],"isStart":false}),makeQuery(id+"F5.opExtrude","CAP_FACE",FACE,{"disambiguationData":[OSD([sQuery(id+"F4.wireOp",EDGE,"E27.bottom"),sQuery(id+"F4.wireOp",EDGE,"E27.top"),sQuery(id+"F4.wireOp",EDGE,"E27.left"),sQuery(id+"F4.wireOp",EDGE,"E27.right")])],"isStart":false})]});
            var sketch = newSketch(context, id + "F39", { "sketchPlane" : qUnion([Q0])});
            skLineSegment(sketch, "E78.0", {"start": v(-7310, -200) * mm, "end": v(200, -200) * mm});
            skLineSegment(sketch, "E79.0", {"start": v(-7310, 1350) * mm, "end": v(-7310, -200) * mm});
            skLineSegment(sketch, "E80.0", {"start": v(-10680, 1350) * mm, "end": v(-7310, 1350) * mm});
            skLineSegment(sketch, "E81.0", {"start": v(-10680, 7400) * mm, "end": v(-10680, 1350) * mm});
            skLineSegment(sketch, "E82.0", {"start": v(-5790, 8000) * mm, "end": v(-10000, 8000) * mm});
            skLineSegment(sketch, "E83.0", {"start": v(-5790, 7350) * mm, "end": v(-5790, 8000) * mm});
            skLineSegment(sketch, "E84.0", {"start": v(710, 7350) * mm, "end": v(-5790, 7350) * mm});
            skLineSegment(sketch, "E85.0", {"start": v(710, 4500) * mm, "end": v(710, 7350) * mm});
            skLineSegment(sketch, "E86.0", {"start": v(2490, 4500) * mm, "end": v(710, 4500) * mm});
            skLineSegment(sketch, "E87.0", {"start": v(2490, 1150) * mm, "end": v(2490, 4500) * mm});
            skLineSegment(sketch, "E88.0", {"start": v(200, 1150) * mm, "end": v(2490, 1150) * mm});
            skLineSegment(sketch, "E89.0", {"start": v(200, -200) * mm, "end": v(200, 1150) * mm});
            skLineSegment(sketch, "E90.0", {"start": v(-10000, 7400) * mm, "end": v(-10680, 7400) * mm});
            skLineSegment(sketch, "E91.0", {"start": v(-10000, 8000) * mm, "end": v(-10000, 7400) * mm});
            skSolve(sketch);
        }
        {
            var Q0;
            Q0=qSketchRegion(id+"F39",true);
            extrude(context, id + "F40", {"entities" : qUnion([Q0]), "depth" : 25 * mm});
        }
        {
            var Q0;
            {var subQ14=makeQuery(id+"F3.opExtrude","CAP_FACE",FACE,{"disambiguationData":[OSD([sQuery(id+"F2.wireOp",EDGE,"E15.0"),sQuery(id+"F2.wireOp",EDGE,"E15.1"),sQuery(id+"F2.wireOp",EDGE,"E15.2"),sQuery(id+"F2.wireOp",EDGE,"E15.3"),sQuery(id+"F2.wireOp",EDGE,"E15.4"),sQuery(id+"F2.wireOp",EDGE,"E15.5"),sQuery(id+"F2.wireOp",EDGE,"E15.6"),sQuery(id+"F2.wireOp",EDGE,"E15.7"),sQuery(id+"F2.wireOp",EDGE,"E15.8"),sQuery(id+"F2.wireOp",EDGE,"E15.9"),sQuery(id+"F2.wireOp",EDGE,"E15.10"),sQuery(id+"F2.wireOp",EDGE,"E15.11"),sQuery(id+"F2.wireOp",EDGE,"E15.12"),sQuery(id+"F2.wireOp",EDGE,"E15.13")])],"isStart":true});var subQ17=sQuery(id+"F4.wireOp",EDGE,"E30.left");var subQ27=sQuery(id+"F4.wireOp",EDGE,"E29.bottom");Q0=makeQuery(id+"F33.boolean.opBoolean","MERGE",FACE,{"derivedFrom":[makeQuery(id+"FckVvop4Cxg8mSC_1.boolean.opBoolean","MERGE",FACE,{"derivedFrom":[makeQuery(id+"F27.boolean.opBoolean","MERGE",FACE,{"derivedFrom":[makeQuery(id+"F5.boolean.opBoolean","SPLIT",FACE,{"disambiguationData":[TD([makeQuery(id+"F5.opExtrude","SWEPT_FACE",FACE,{"disambiguationData":[OSD([subQ27])]})])],"derivedFrom":subQ14}),makeQuery(id+"F5.boolean.opBoolean","SPLIT",FACE,{"disambiguationData":[TD([makeQuery(id+"F1.opExtrude","SWEPT_FACE",FACE,{"disambiguationData":[OSD([sQuery(id+"F0.wireOp",EDGE,"E11")])]})])],"derivedFrom":subQ14}),makeQuery(id+"F27.opExtrude","SWEPT_FACE",FACE,{"disambiguationData":[OSD([sQuery(id+"F26.wireOp",EDGE,"E64.top")])]})]}),makeQuery(id+"F6zg25L2LszjJW5_1.boolean.opBoolean","MERGE",FACE,{"derivedFrom":[makeQuery(id+"F5.boolean.opBoolean","SPLIT",FACE,{"disambiguationData":[TD([makeQuery(id+"F1.opExtrude","SWEPT_FACE",FACE,{"disambiguationData":[OSD([sQuery(id+"F0.wireOp",EDGE,"E6")])]})])],"derivedFrom":subQ14}),makeQuery(id+"F5.boolean.opBoolean","SPLIT",FACE,{"disambiguationData":[TD([makeQuery(id+"F1.opExtrude","SWEPT_FACE",FACE,{"disambiguationData":[OSD([sQuery(id+"F0.wireOp",EDGE,"E8")])]})])],"derivedFrom":subQ14}),makeQuery(id+"F31.boolean.opBoolean","MERGE",FACE,{"derivedFrom":[makeQuery(id+"F29.boolean.opBoolean","MERGE",FACE,{"derivedFrom":[makeQuery(id+"F5.boolean.opBoolean","SPLIT",FACE,{"disambiguationData":[TD([makeQuery(id+"F5.opExtrude","SWEPT_FACE",FACE,{"disambiguationData":[OSD([subQ17])]})])],"derivedFrom":subQ14}),makeQuery(id+"F5.boolean.opBoolean","SPLIT",FACE,{"disambiguationData":[TD([makeQuery(id+"F1.opExtrude","SWEPT_FACE",FACE,{"disambiguationData":[OSD([sQuery(id+"F0.wireOp",EDGE,"E12")])]})])],"derivedFrom":subQ14}),makeQuery(id+"F5.boolean.opBoolean","SPLIT",FACE,{"disambiguationData":[TD([makeQuery(id+"F1.opExtrude","SWEPT_FACE",FACE,{"disambiguationData":[OSD([sQuery(id+"F0.wireOp",EDGE,"E0")])]})])],"derivedFrom":subQ14}),makeQuery(id+"F29.opExtrude","SWEPT_FACE",FACE,{"disambiguationData":[OSD([sQuery(id+"F28.wireOp",EDGE,"E65.top")])]})]}),makeQuery(id+"F31.opExtrude","SWEPT_FACE",FACE,{"disambiguationData":[OSD([sQuery(id+"F30.wireOp",EDGE,"E66.top")])]})]}),makeQuery(id+"F6zg25L2LszjJW5_1.opExtrude","SWEPT_FACE",FACE,{"disambiguationData":[OSD([sQuery(id+"FWPBm3OvsiiB5Cd_1.wireOp",EDGE,"69Jxp35O-uAKO-hYMn-1soW-FQlsPvDcRQSu.top")])]})]}),makeQuery(id+"FckVvop4Cxg8mSC_1.opExtrude","SWEPT_FACE",FACE,{"disambiguationData":[OSD([sQuery(id+"FyAG4XqI51y0cRb_1.wireOp",EDGE,"nZ2zRKJ4-6J7Y-40UK-3UeH-tHKudJzRdtMp.top")])]})]}),makeQuery(id+"F33.opExtrude","SWEPT_FACE",FACE,{"disambiguationData":[OSD([sQuery(id+"F32.wireOp",EDGE,"E67.top")])]})]});}
            cPlane(context, id + "F41", {"entities" : qUnion([Q0]), "cplaneType" : CPlaneType.OFFSET, "offset" : 1300 * mm, "width" : 150 * mm, "height" : 150 * mm});
        }
        {
            var Q0;
            Q0=qCreatedBy(id+"F41.planeOp",FACE);
            var sketch = newSketch(context, id + "F42", { "sketchPlane" : qUnion([Q0])});
            skCircle(sketch, "E92", {"center": v(-6460, 350) * mm, "radius": 350 * mm});
            skSolve(sketch);
        }
        {
            var Q0;
            Q0=qSketchRegion(id+"F42",true);
            extrude(context, id + "F43", {"entities" : qUnion([Q0]), "operationType" : NewBodyOperationType.ADD, "depth" : 1000 * mm});
        }
        {
            var Q0;
            {var subQ14=makeQuery(id+"F3.opExtrude","CAP_FACE",FACE,{"disambiguationData":[OSD([sQuery(id+"F2.wireOp",EDGE,"E15.0"),sQuery(id+"F2.wireOp",EDGE,"E15.1"),sQuery(id+"F2.wireOp",EDGE,"E15.2"),sQuery(id+"F2.wireOp",EDGE,"E15.3"),sQuery(id+"F2.wireOp",EDGE,"E15.4"),sQuery(id+"F2.wireOp",EDGE,"E15.5"),sQuery(id+"F2.wireOp",EDGE,"E15.6"),sQuery(id+"F2.wireOp",EDGE,"E15.7"),sQuery(id+"F2.wireOp",EDGE,"E15.8"),sQuery(id+"F2.wireOp",EDGE,"E15.9"),sQuery(id+"F2.wireOp",EDGE,"E15.10"),sQuery(id+"F2.wireOp",EDGE,"E15.11"),sQuery(id+"F2.wireOp",EDGE,"E15.12"),sQuery(id+"F2.wireOp",EDGE,"E15.13")])],"isStart":true});var subQ17=sQuery(id+"F4.wireOp",EDGE,"E30.left");var subQ27=sQuery(id+"F4.wireOp",EDGE,"E29.bottom");Q0=makeQuery(id+"F33.boolean.opBoolean","MERGE",FACE,{"derivedFrom":[makeQuery(id+"FckVvop4Cxg8mSC_1.boolean.opBoolean","MERGE",FACE,{"derivedFrom":[makeQuery(id+"F27.boolean.opBoolean","MERGE",FACE,{"derivedFrom":[makeQuery(id+"F5.boolean.opBoolean","SPLIT",FACE,{"disambiguationData":[TD([makeQuery(id+"F5.opExtrude","SWEPT_FACE",FACE,{"disambiguationData":[OSD([subQ27])]})])],"derivedFrom":subQ14}),makeQuery(id+"F5.boolean.opBoolean","SPLIT",FACE,{"disambiguationData":[TD([makeQuery(id+"F1.opExtrude","SWEPT_FACE",FACE,{"disambiguationData":[OSD([sQuery(id+"F0.wireOp",EDGE,"E11")])]})])],"derivedFrom":subQ14}),makeQuery(id+"F27.opExtrude","SWEPT_FACE",FACE,{"disambiguationData":[OSD([sQuery(id+"F26.wireOp",EDGE,"E64.top")])]})]}),makeQuery(id+"F6zg25L2LszjJW5_1.boolean.opBoolean","MERGE",FACE,{"derivedFrom":[makeQuery(id+"F5.boolean.opBoolean","SPLIT",FACE,{"disambiguationData":[TD([makeQuery(id+"F1.opExtrude","SWEPT_FACE",FACE,{"disambiguationData":[OSD([sQuery(id+"F0.wireOp",EDGE,"E6")])]})])],"derivedFrom":subQ14}),makeQuery(id+"F5.boolean.opBoolean","SPLIT",FACE,{"disambiguationData":[TD([makeQuery(id+"F1.opExtrude","SWEPT_FACE",FACE,{"disambiguationData":[OSD([sQuery(id+"F0.wireOp",EDGE,"E8")])]})])],"derivedFrom":subQ14}),makeQuery(id+"F31.boolean.opBoolean","MERGE",FACE,{"derivedFrom":[makeQuery(id+"F29.boolean.opBoolean","MERGE",FACE,{"derivedFrom":[makeQuery(id+"F5.boolean.opBoolean","SPLIT",FACE,{"disambiguationData":[TD([makeQuery(id+"F5.opExtrude","SWEPT_FACE",FACE,{"disambiguationData":[OSD([subQ17])]})])],"derivedFrom":subQ14}),makeQuery(id+"F5.boolean.opBoolean","SPLIT",FACE,{"disambiguationData":[TD([makeQuery(id+"F1.opExtrude","SWEPT_FACE",FACE,{"disambiguationData":[OSD([sQuery(id+"F0.wireOp",EDGE,"E12")])]})])],"derivedFrom":subQ14}),makeQuery(id+"F5.boolean.opBoolean","SPLIT",FACE,{"disambiguationData":[TD([makeQuery(id+"F1.opExtrude","SWEPT_FACE",FACE,{"disambiguationData":[OSD([sQuery(id+"F0.wireOp",EDGE,"E0")])]})])],"derivedFrom":subQ14}),makeQuery(id+"F29.opExtrude","SWEPT_FACE",FACE,{"disambiguationData":[OSD([sQuery(id+"F28.wireOp",EDGE,"E65.top")])]})]}),makeQuery(id+"F31.opExtrude","SWEPT_FACE",FACE,{"disambiguationData":[OSD([sQuery(id+"F30.wireOp",EDGE,"E66.top")])]})]}),makeQuery(id+"F6zg25L2LszjJW5_1.opExtrude","SWEPT_FACE",FACE,{"disambiguationData":[OSD([sQuery(id+"FWPBm3OvsiiB5Cd_1.wireOp",EDGE,"69Jxp35O-uAKO-hYMn-1soW-FQlsPvDcRQSu.top")])]})]}),makeQuery(id+"FckVvop4Cxg8mSC_1.opExtrude","SWEPT_FACE",FACE,{"disambiguationData":[OSD([sQuery(id+"FyAG4XqI51y0cRb_1.wireOp",EDGE,"nZ2zRKJ4-6J7Y-40UK-3UeH-tHKudJzRdtMp.top")])]})]}),makeQuery(id+"F33.opExtrude","SWEPT_FACE",FACE,{"disambiguationData":[OSD([sQuery(id+"F32.wireOp",EDGE,"E67.top")])]})]});}
            var sketch = newSketch(context, id + "F44", { "sketchPlane" : qUnion([Q0])});
            skLineSegment(sketch, "E93.bottom", {"start": v(-3610, 3260) * mm, "end": v(-4097.34, 3260) * mm});
            skLineSegment(sketch, "E93.top", {"start": v(-3610, 1680) * mm, "end": v(-4097.34, 1680) * mm});
            skLineSegment(sketch, "E93.left", {"start": v(-3610, 3260) * mm, "end": v(-3610, 1680) * mm});
            skLineSegment(sketch, "E93.right", {"start": v(-4097.34, 3260) * mm, "end": v(-4097.34, 1680) * mm});
            skLineSegment(sketch, "E94.bottom", {"start": v(-7020, 3410) * mm, "end": v(-5470, 3410) * mm});
            skLineSegment(sketch, "E94.top", {"start": v(-7020, 2922.66) * mm, "end": v(-5470, 2922.66) * mm});
            skLineSegment(sketch, "E94.left", {"start": v(-7020, 3410) * mm, "end": v(-7020, 2922.66) * mm});
            skLineSegment(sketch, "E94.right", {"start": v(-5470, 3410) * mm, "end": v(-5470, 2922.66) * mm});
            skSolve(sketch);
        }
        {
            var Q0;
            Q0=qSketchRegion(id+"F44",true);
            extrude(context, id + "F45", {"entities" : qUnion([Q0]), "depth" : 700 * mm});
        }
        {
            var Q0;
            Q0=makeQuery(id+"F45.opExtrude","CAP_FACE",FACE,{"disambiguationData":[OSD([sQuery(id+"F44.wireOp",EDGE,"E94.bottom"),sQuery(id+"F44.wireOp",EDGE,"E94.top"),sQuery(id+"F44.wireOp",EDGE,"E94.left"),sQuery(id+"F44.wireOp",EDGE,"E94.right")])],"isStart":false});
            var sketch = newSketch(context, id + "F46", { "sketchPlane" : qUnion([Q0])});
            skLineSegment(sketch, "E95.0.0", {"start": v(-3610, 3260) * mm, "end": v(-4097.34, 3260) * mm, "construction": true});
            skLineSegment(sketch, "E95.0.1", {"start": v(-4097.34, 3260) * mm, "end": v(-4097.34, 1680) * mm, "construction": true});
            skLineSegment(sketch, "E95.0.2", {"start": v(-4097.34, 1680) * mm, "end": v(-3610, 1680) * mm, "construction": true});
            skLineSegment(sketch, "E95.0.3", {"start": v(-3610, 1680) * mm, "end": v(-3610, 3260) * mm, "construction": true});
            skLineSegment(sketch, "E96.0", {"start": v(-3710, 1830) * mm, "end": v(-3710, 3110) * mm});
            skLineSegment(sketch, "E96.1", {"start": v(-3947.34, 1780) * mm, "end": v(-3760, 1780) * mm});
            skLineSegment(sketch, "E96.2", {"start": v(-3997.34, 3110) * mm, "end": v(-3997.34, 1830) * mm});
            skLineSegment(sketch, "E96.3", {"start": v(-3760, 3160) * mm, "end": v(-3947.34, 3160) * mm});
            skPoint(sketch, "E97.visualSharp", {"position": v(-3997.34, 3160) * mm});
            skArc(sketch, "E97.filletArc", {"start": v(-3947.34, 3160) * mm, "mid": v(-3982.7, 3145.36) * mm, "end": v(-3997.34, 3110) * mm});
            skPoint(sketch, "E98.visualSharp", {"position": v(-3710, 1780) * mm});
            skArc(sketch, "E98.filletArc", {"start": v(-3760, 1780) * mm, "mid": v(-3724.64, 1794.64) * mm, "end": v(-3710, 1830) * mm});
            skPoint(sketch, "E99.visualSharp", {"position": v(-3997.34, 1780) * mm});
            skArc(sketch, "E99.filletArc", {"start": v(-3997.34, 1830) * mm, "mid": v(-3982.7, 1794.64) * mm, "end": v(-3947.34, 1780) * mm});
            skPoint(sketch, "E100.visualSharp", {"position": v(-3710, 3160) * mm});
            skArc(sketch, "E100.filletArc", {"start": v(-3710, 3110) * mm, "mid": v(-3724.64, 3145.36) * mm, "end": v(-3760, 3160) * mm});
            skSolve(sketch);
        }
        {
            var Q0;
            Q0=qSketchRegion(id+"F46",true);
            extrude(context, id + "F47", {"entities" : qUnion([Q0]), "operationType" : NewBodyOperationType.REMOVE, "oppositeDirection" : true, "depth" : 500 * mm});
        }
        {
            var Q0;
            Q0=makeQuery(id+"F45.opExtrude","CAP_FACE",FACE,{"disambiguationData":[OSD([sQuery(id+"F44.wireOp",EDGE,"E94.bottom"),sQuery(id+"F44.wireOp",EDGE,"E94.top"),sQuery(id+"F44.wireOp",EDGE,"E94.left"),sQuery(id+"F44.wireOp",EDGE,"E94.right")])],"isStart":false});
            var sketch = newSketch(context, id + "F48", { "sketchPlane" : qUnion([Q0])});
            skLineSegment(sketch, "E101.0.0", {"start": v(-7020, 3410) * mm, "end": v(-7020, 2922.66) * mm, "construction": true});
            skLineSegment(sketch, "E101.0.1", {"start": v(-7020, 2922.66) * mm, "end": v(-5470, 2922.66) * mm, "construction": true});
            skLineSegment(sketch, "E101.0.2", {"start": v(-5470, 2922.66) * mm, "end": v(-5470, 3410) * mm, "construction": true});
            skLineSegment(sketch, "E101.0.3", {"start": v(-5470, 3410) * mm, "end": v(-7020, 3410) * mm, "construction": true});
            skLineSegment(sketch, "E102.0", {"start": v(-5600, 3330) * mm, "end": v(-6890, 3330) * mm});
            skLineSegment(sketch, "E102.1", {"start": v(-5550, 3052.66) * mm, "end": v(-5550, 3280) * mm});
            skLineSegment(sketch, "E102.2", {"start": v(-6890, 3002.66) * mm, "end": v(-5600, 3002.66) * mm});
            skLineSegment(sketch, "E102.3", {"start": v(-6940, 3280) * mm, "end": v(-6940, 3052.66) * mm});
            skPoint(sketch, "E103.visualSharp", {"position": v(-6940, 3330) * mm});
            skArc(sketch, "E103.filletArc", {"start": v(-6890, 3330) * mm, "mid": v(-6925.36, 3315.36) * mm, "end": v(-6940, 3280) * mm});
            skPoint(sketch, "E104.visualSharp", {"position": v(-5550, 3330) * mm});
            skArc(sketch, "E104.filletArc", {"start": v(-5550, 3280) * mm, "mid": v(-5564.64, 3315.36) * mm, "end": v(-5600, 3330) * mm});
            skPoint(sketch, "E105.visualSharp", {"position": v(-5550, 3002.66) * mm});
            skArc(sketch, "E105.filletArc", {"start": v(-5600, 3002.66) * mm, "mid": v(-5564.64, 3017.3) * mm, "end": v(-5550, 3052.66) * mm});
            skPoint(sketch, "E106.visualSharp", {"position": v(-6940, 3002.66) * mm});
            skArc(sketch, "E106.filletArc", {"start": v(-6940, 3052.66) * mm, "mid": v(-6925.36, 3017.3) * mm, "end": v(-6890, 3002.66) * mm});
            skSolve(sketch);
        }
        {
            var Q0;
            Q0=qSketchRegion(id+"F48",true);
            extrude(context, id + "F49", {"entities" : qUnion([Q0]), "operationType" : NewBodyOperationType.REMOVE, "oppositeDirection" : true, "depth" : 500 * mm});
        }
    });
